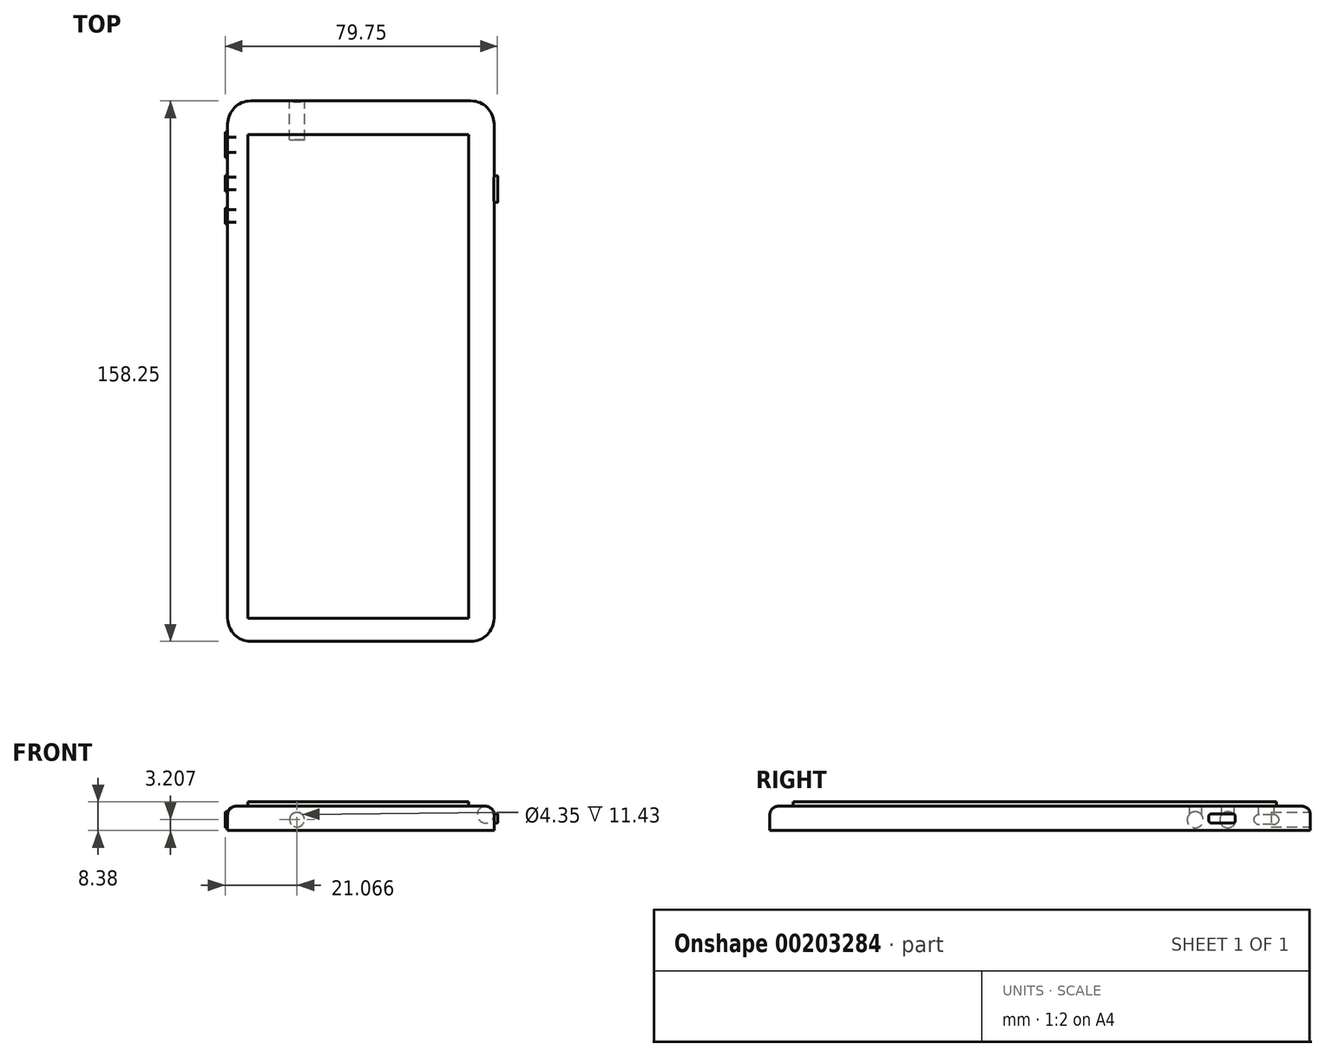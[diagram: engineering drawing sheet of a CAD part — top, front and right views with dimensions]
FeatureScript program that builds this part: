
annotation { "Feature Type Name" : "Feature", "Feature Type Description" : "" }
export const myFeature = defineFeature(function(context is Context, id is Id, definition is map)
    precondition{}
    {
        {
            var Q0;
            Q0=qCreatedBy(makeId("Top.planeOp"),FACE);
            var sketch = newSketch(context, id + "F0", { "sketchPlane" : qUnion([Q0])});
            skLineSegment(sketch, "E0.bottom", {"start": v(-57.2, 79.59) * mm, "end": v(20.77, 79.59) * mm});
            skLineSegment(sketch, "E0.top", {"start": v(-57.2, -78.66) * mm, "end": v(20.77, -78.66) * mm});
            skLineSegment(sketch, "E0.left", {"start": v(-57.2, 79.59) * mm, "end": v(-57.2, -78.66) * mm});
            skLineSegment(sketch, "E0.right", {"start": v(20.77, 79.59) * mm, "end": v(20.77, -78.66) * mm});
            skLineSegment(sketch, "E1.bottom", {"start": v(-50.78, 73.22) * mm, "end": v(13.84, 73.22) * mm});
            skLineSegment(sketch, "E1.top", {"start": v(-50.78, -72.28) * mm, "end": v(13.84, -72.28) * mm});
            skLineSegment(sketch, "E1.left", {"start": v(-50.78, 73.22) * mm, "end": v(-50.78, -72.28) * mm});
            skLineSegment(sketch, "E1.right", {"start": v(13.84, 73.22) * mm, "end": v(13.84, -72.28) * mm});
            skSolve(sketch);
        }
        {
            var Q0;
            Q0=makeQuery(id+"F0.imprint","IMPRINT",FACE,{"disambiguationData":[TD([[makeQuery(id+"F0.imprint","IMPRINT",EDGE,{"derivedFrom":sQuery(id+"F0.wireOp",EDGE,"E0.bottom")}),-1.0]])]});
            extrude(context, id + "F1", {"entities" : qUnion([Q0]), "depth" : 7.11 * mm});
        }
        {
            var Q0;
            Q0=makeQuery(id+"F1.opExtrude","SWEPT_FACE",FACE,{"disambiguationData":[OSD([sQuery(id+"F0.wireOp",EDGE,"E1.bottom")])]});
            var Q1;
            Q1=makeQuery(id+"F1.opExtrude","SWEPT_FACE",FACE,{"disambiguationData":[OSD([sQuery(id+"F0.wireOp",EDGE,"E1.top")])]});
            extrude(context, id + "F2", {"entities" : qUnion([Q0]), "operationType" : NewBodyOperationType.ADD, "endBound" : BoundingType.UP_TO_SURFACE, "endBoundEntityFace" : qUnion([Q1]), "depth" : 25.4 * mm});
        }
        {
            var Q0;
            {var subQ0=sQuery(id+"F0.wireOp",EDGE,"E1.bottom");Q0=makeQuery(id+"F2.boolean.opBoolean","MERGE",FACE,{"derivedFrom":[makeQuery(id+"F1.opExtrude","CAP_FACE",FACE,{"disambiguationData":[OSD([sQuery(id+"F0.wireOp",EDGE,"E0.bottom"),sQuery(id+"F0.wireOp",EDGE,"E0.top"),sQuery(id+"F0.wireOp",EDGE,"E0.left"),sQuery(id+"F0.wireOp",EDGE,"E0.right"),subQ0,sQuery(id+"F0.wireOp",EDGE,"E1.top"),sQuery(id+"F0.wireOp",EDGE,"E1.left"),sQuery(id+"F0.wireOp",EDGE,"E1.right"),sQuery(id+"F0.wireOp",EDGE,"hBJIGxE4-hDb8-UbeB-YG6C-1WGc27omxzX5")])],"isStart":false}),makeQuery(id+"F2.opExtrude","SWEPT_FACE",FACE,{"disambiguationData":[OSD([subQ0]),TDD([makeQuery(id+"F1.opExtrude","CAP_EDGE",EDGE,{"disambiguationData":[OSD([subQ0])],"isStart":false})])]})]});}
            var sketch = newSketch(context, id + "F3", { "sketchPlane" : qUnion([Q0])});
            skLineSegment(sketch, "E2.bottom", {"start": v(-51.3, 69.69) * mm, "end": v(13.33, 69.69) * mm});
            skLineSegment(sketch, "E2.top", {"start": v(-51.3, -71.84) * mm, "end": v(13.33, -71.84) * mm});
            skLineSegment(sketch, "E2.left", {"start": v(-51.3, 69.69) * mm, "end": v(-51.3, -71.84) * mm});
            skLineSegment(sketch, "E2.right", {"start": v(13.33, 69.69) * mm, "end": v(13.33, -71.84) * mm});
            skSolve(sketch);
        }
        {
            var Q0;
            Q0=makeQuery(id+"F3.imprint","IMPRINT",FACE,{"disambiguationData":[TD([[makeQuery(id+"F3.imprint","IMPRINT",EDGE,{"derivedFrom":sQuery(id+"F3.wireOp",EDGE,"E2.bottom")}),-1.0]])]});
            extrude(context, id + "F4", {"entities" : qUnion([Q0]), "operationType" : NewBodyOperationType.ADD, "depth" : 1.27 * mm});
        }
        {
            var Q0;
            Q0=makeQuery(id+"F1.opExtrude","SWEPT_EDGE",EDGE,{"disambiguationData":[OSD([sQuery(id+"F0.wireOp",EDGE,"E0.top"),sQuery(id+"F0.wireOp",EDGE,"E0.right")])]});
            var Q1;
            Q1=makeQuery(id+"F1.opExtrude","SWEPT_EDGE",EDGE,{"disambiguationData":[OSD([sQuery(id+"F0.wireOp",EDGE,"E0.top"),sQuery(id+"F0.wireOp",EDGE,"E0.left")])]});
            var Q2;
            Q2=makeQuery(id+"F1.opExtrude","SWEPT_EDGE",EDGE,{"disambiguationData":[OSD([sQuery(id+"F0.wireOp",EDGE,"E0.bottom"),sQuery(id+"F0.wireOp",EDGE,"E0.left")])]});
            var Q3;
            Q3=makeQuery(id+"F1.opExtrude","SWEPT_EDGE",EDGE,{"disambiguationData":[OSD([sQuery(id+"F0.wireOp",EDGE,"E0.bottom"),sQuery(id+"F0.wireOp",EDGE,"E0.right")])]});
            fillet(context, id + "F5", {"entities" : qUnion([Q0, Q1, Q2, Q3]), "radius" : 6.75 * mm, "tangentPropagation" : true, "allowEdgeOverflow" : false});
        }
        {
            var Q0;
            Q0=makeQuery(id+"F1.opExtrude","SWEPT_FACE",FACE,{"disambiguationData":[OSD([sQuery(id+"F0.wireOp",EDGE,"E0.left")])]});
            var sketch = newSketch(context, id + "F6", { "sketchPlane" : qUnion([Q0])});
            skCircle(sketch, "E3", {"center": v(-55.43, 3.15) * mm, "radius": 2.35 * mm});
            skCircle(sketch, "E4", {"center": v(-45.88, 3.15) * mm, "radius": 2.35 * mm});
            skLineSegment(sketch, "E5.bottom", {"start": v(-70.53, 4.68) * mm, "end": v(-62.91, 4.68) * mm});
            skLineSegment(sketch, "E5.top", {"start": v(-70.53, 1.77) * mm, "end": v(-62.91, 1.77) * mm});
            skLineSegment(sketch, "E5.left", {"start": v(-70.53, 4.68) * mm, "end": v(-70.53, 1.77) * mm});
            skLineSegment(sketch, "E5.right", {"start": v(-62.91, 4.68) * mm, "end": v(-62.91, 1.77) * mm});
            skSolve(sketch);
        }
        {
            var Q0;
            Q0=makeQuery(id+"F1.opExtrude","SWEPT_FACE",FACE,{"disambiguationData":[OSD([sQuery(id+"F0.wireOp",EDGE,"E0.bottom")])]});
            var sketch = newSketch(context, id + "F7", { "sketchPlane" : qUnion([Q0])});
            skCircle(sketch, "E6", {"center": v(36.9, 3.2) * mm, "radius": 2.18 * mm});
            skSolve(sketch);
        }
        {
            var Q0;
            Q0=makeQuery(id+"F1.opExtrude","SWEPT_FACE",FACE,{"disambiguationData":[OSD([sQuery(id+"F0.wireOp",EDGE,"E0.right")])]});
            var sketch = newSketch(context, id + "F8", { "sketchPlane" : qUnion([Q0])});
            skLineSegment(sketch, "E7.bottom", {"start": v(49.88, 4.88) * mm, "end": v(57.62, 4.88) * mm});
            skLineSegment(sketch, "E7.top", {"start": v(49.88, 2.23) * mm, "end": v(57.62, 2.23) * mm});
            skLineSegment(sketch, "E7.left", {"start": v(49.88, 4.88) * mm, "end": v(49.88, 2.23) * mm});
            skLineSegment(sketch, "E7.right", {"start": v(57.62, 4.88) * mm, "end": v(57.62, 2.23) * mm});
            skSolve(sketch);
        }
        {
            var Q0;
            Q0=makeQuery(id+"F6.imprint","IMPRINT",FACE,{"disambiguationData":[TD([[makeQuery(id+"F6.imprint","IMPRINT",EDGE,{"derivedFrom":sQuery(id+"F6.wireOp",EDGE,"E5.bottom")}),-1.0]])]});
            var Q1;
            Q1=makeQuery(id+"F6.imprint","IMPRINT",FACE,{"disambiguationData":[TD([[makeQuery(id+"F6.imprint","IMPRINT",EDGE,{"derivedFrom":sQuery(id+"F6.wireOp",EDGE,"E3")}),1.0]])]});
            var Q2;
            Q2=makeQuery(id+"F6.imprint","IMPRINT",FACE,{"disambiguationData":[TD([[makeQuery(id+"F6.imprint","IMPRINT",EDGE,{"derivedFrom":sQuery(id+"F6.wireOp",EDGE,"E4")}),1.0]])]});
            extrude(context, id + "F9", {"entities" : qUnion([Q0, Q1, Q2]), "operationType" : NewBodyOperationType.ADD, "depth" : 25.4 * mm});
        }
        {
            var Q0;
            Q0=makeQuery(id+"F9.opExtrude","SWEPT_EDGE",EDGE,{"disambiguationData":[OSD([sQuery(id+"F6.wireOp",EDGE,"E5.top"),sQuery(id+"F6.wireOp",EDGE,"E5.right")])]});
            var Q1;
            Q1=makeQuery(id+"F9.opExtrude","SWEPT_EDGE",EDGE,{"disambiguationData":[OSD([sQuery(id+"F6.wireOp",EDGE,"E5.top"),sQuery(id+"F6.wireOp",EDGE,"E5.left")])]});
            var Q2;
            Q2=makeQuery(id+"F9.opExtrude","SWEPT_EDGE",EDGE,{"disambiguationData":[OSD([sQuery(id+"F6.wireOp",EDGE,"E5.bottom"),sQuery(id+"F6.wireOp",EDGE,"E5.left")])]});
            var Q3;
            Q3=makeQuery(id+"F9.opExtrude","SWEPT_EDGE",EDGE,{"disambiguationData":[OSD([sQuery(id+"F6.wireOp",EDGE,"E5.bottom"),sQuery(id+"F6.wireOp",EDGE,"E5.right")])]});
            fillet(context, id + "F10", {"entities" : qUnion([Q0, Q1, Q2, Q3]), "radius" : 1.84 * mm, "tangentPropagation" : true, "allowEdgeOverflow" : false});
        }
        {
            var Q0;
            Q0=makeQuery(id+"F9.opExtrude","CAP_FACE",FACE,{"disambiguationData":[OSD([sQuery(id+"F6.wireOp",EDGE,"E5.bottom"),sQuery(id+"F6.wireOp",EDGE,"E5.top"),sQuery(id+"F6.wireOp",EDGE,"E5.left"),sQuery(id+"F6.wireOp",EDGE,"E5.right")])],"isStart":false});
            var Q1;
            Q1=makeQuery(id+"F9.opExtrude","CAP_FACE",FACE,{"disambiguationData":[OSD([sQuery(id+"F6.wireOp",EDGE,"E3")])],"isStart":false});
            var Q2;
            Q2=makeQuery(id+"F9.opExtrude","CAP_FACE",FACE,{"disambiguationData":[OSD([sQuery(id+"F6.wireOp",EDGE,"E4")])],"isStart":false});
            extrude(context, id + "F11", {"entities" : qUnion([Q0, Q1, Q2]), "operationType" : NewBodyOperationType.REMOVE, "oppositeDirection" : true, "depth" : 24.64 * mm});
        }
        {
            var Q0;
            Q0=makeQuery(id+"F8.imprint","IMPRINT",FACE,{"disambiguationData":[TD([[makeQuery(id+"F8.imprint","IMPRINT",EDGE,{"derivedFrom":sQuery(id+"F8.wireOp",EDGE,"E7.bottom")}),-1.0]])]});
            extrude(context, id + "F12", {"entities" : qUnion([Q0]), "operationType" : NewBodyOperationType.ADD, "depth" : 1.02 * mm});
        }
        {
            var Q0;
            Q0=makeQuery(id+"F7.imprint","IMPRINT",FACE,{"disambiguationData":[TD([[makeQuery(id+"F7.imprint","IMPRINT",EDGE,{"derivedFrom":sQuery(id+"F7.wireOp",EDGE,"E6")}),1.0]])]});
            extrude(context, id + "F13", {"entities" : qUnion([Q0]), "operationType" : NewBodyOperationType.REMOVE, "oppositeDirection" : true, "depth" : 11.43 * mm});
        }
        {
            var Q0;
            Q0=makeQuery(id+"F1.opExtrude","CAP_EDGE",EDGE,{"disambiguationData":[OSD([sQuery(id+"F0.wireOp",EDGE,"E0.left")])],"isStart":false});
            fillet(context, id + "F14", {"entities" : qUnion([Q0]), "radius" : 2.45 * mm, "tangentPropagation" : true, "allowEdgeOverflow" : false});
        }
        {
            var Q0;
            Q0=makeQuery(id+"F12.opExtrude","SWEPT_EDGE",EDGE,{"disambiguationData":[OSD([sQuery(id+"F8.wireOp",EDGE,"E7.bottom"),sQuery(id+"F8.wireOp",EDGE,"E7.right")])]});
            var Q1;
            Q1=makeQuery(id+"F12.opExtrude","SWEPT_EDGE",EDGE,{"disambiguationData":[OSD([sQuery(id+"F8.wireOp",EDGE,"E7.top"),sQuery(id+"F8.wireOp",EDGE,"E7.right")])]});
            var Q2;
            Q2=makeQuery(id+"F12.opExtrude","SWEPT_EDGE",EDGE,{"disambiguationData":[OSD([sQuery(id+"F8.wireOp",EDGE,"E7.top"),sQuery(id+"F8.wireOp",EDGE,"E7.left")])]});
            var Q3;
            Q3=makeQuery(id+"F12.opExtrude","SWEPT_EDGE",EDGE,{"disambiguationData":[OSD([sQuery(id+"F8.wireOp",EDGE,"E7.bottom"),sQuery(id+"F8.wireOp",EDGE,"E7.left")])]});
            fillet(context, id + "F15", {"entities" : qUnion([Q0, Q1, Q2, Q3]), "radius" : 0.67 * mm, "tangentPropagation" : true, "allowEdgeOverflow" : false});
        }
    });
